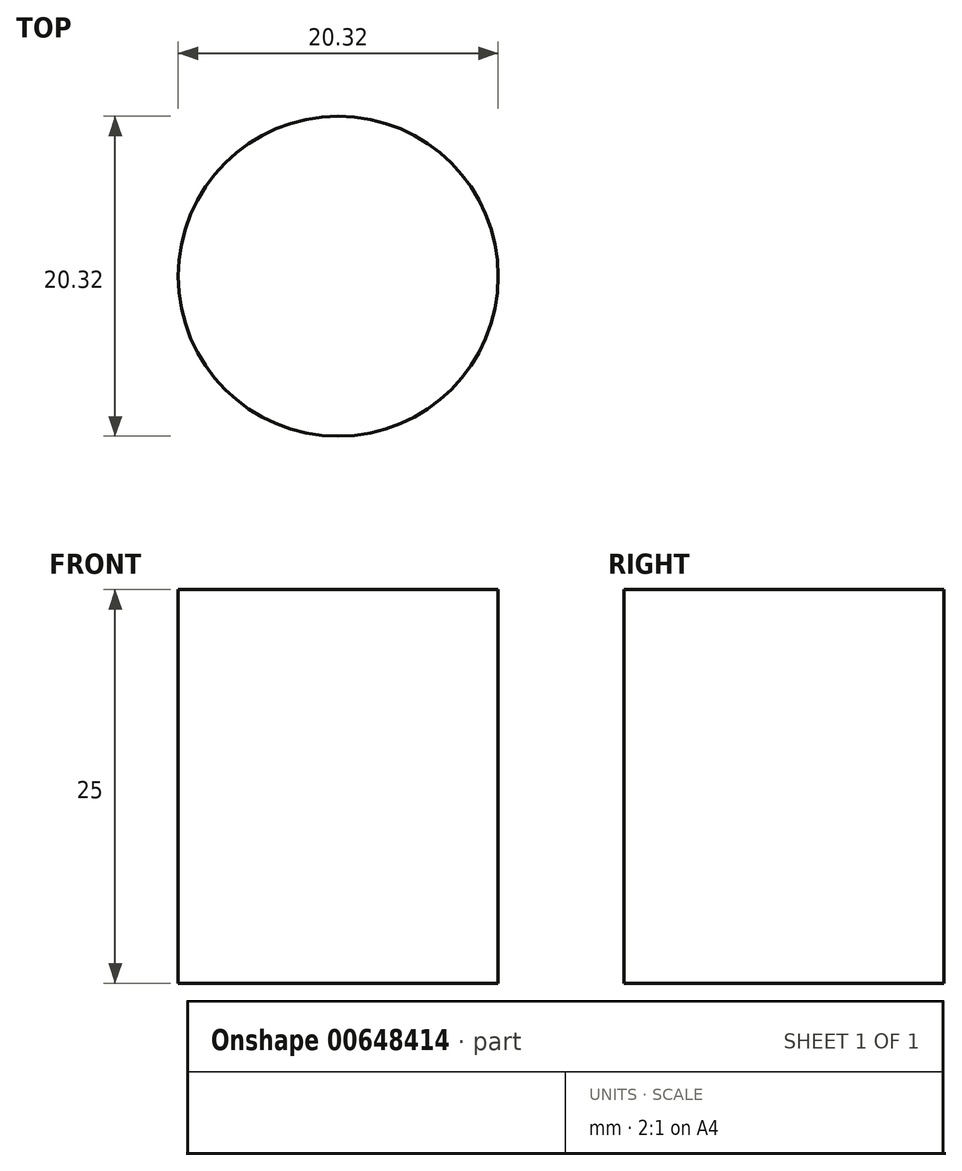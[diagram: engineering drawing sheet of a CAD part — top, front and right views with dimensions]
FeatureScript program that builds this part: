
annotation { "Feature Type Name" : "Feature", "Feature Type Description" : "" }
export const myFeature = defineFeature(function(context is Context, id is Id, definition is map)
    precondition{}
    {
        {
            var Q0;
            Q0=qCreatedBy(makeId("Top.planeOp"),FACE);
            var sketch = newSketch(context, id + "F0", { "sketchPlane" : qUnion([Q0])});
            skLineSegment(sketch, "E0.bottom", {"start": v(-40, -40) * mm, "end": v(40, -40) * mm, "construction": true});
            skLineSegment(sketch, "E0.top", {"start": v(-40, 40) * mm, "end": v(40, 40) * mm, "construction": true});
            skLineSegment(sketch, "E0.left", {"start": v(-40, -40) * mm, "end": v(-40, 40) * mm, "construction": true});
            skLineSegment(sketch, "E0.right", {"start": v(40, -40) * mm, "end": v(40, 40) * mm, "construction": true});
            skPoint(sketch, "E0.middle", {"position": v(0, 0) * mm});
            skCircle(sketch, "E1", {"center": v(40, 40) * mm, "radius": 7 * mm});
            skCircle(sketch, "E2", {"center": v(40, 40) * mm, "radius": 10.16 * mm});
            skLineSegment(sketch, "E3", {"start": v(23.61, 0) * mm, "end": v(23.61, 15.35) * mm});
            skLineSegment(sketch, "E4", {"start": v(22.84, 15.35) * mm, "end": v(14, 22.89) * mm});
            skLineSegment(sketch, "E5", {"start": v(14, 22.89) * mm, "end": v(12.44, 31.72) * mm});
            skLineSegment(sketch, "E6", {"start": v(12.44, 31.72) * mm, "end": v(34.1, 31.72) * mm});
            skLineSegment(sketch, "E7", {"start": v(34.1, 31.72) * mm, "end": v(128.15, 50) * mm});
            skSolve(sketch);
        }
        {
            var Q0;
            Q0=makeQuery(id+"F0.imprint","IMPRINT",FACE,{"disambiguationData":[TD([[makeQuery(id+"F0.imprint","IMPRINT",EDGE,{"derivedFrom":sQuery(id+"F0.wireOp",EDGE,"E1")}),1.0]])]});
            var Q1;
            {var subQ0=sQuery(id+"F0.wireOp",EDGE,"E1");Q1=makeQuery(id+"F0.imprint","IMPRINT",FACE,{"disambiguationData":[TD([[makeQuery(id+"F0.imprint","IMPRINT",EDGE,{"derivedFrom":subQ0}),-1.0]])]});}
            var Q2;
            {var subQ0=sQuery(id+"F0.wireOp",EDGE,"E7");var subQ1=sQuery(id+"F0.wireOp",EDGE,"E2");var subQ2=makeQuery(id+"F0.imprint","INTERSECT",VERTEX,{"disambiguationData":[OD(0.0)],"derivedFrom":[subQ1,subQ0]});Q2=makeQuery(id+"F0.imprint","IMPRINT",FACE,{"disambiguationData":[TD([[makeQuery(id+"F0.imprint","IMPRINT",EDGE,{"disambiguationData":[TD([[subQ2,-1.0]])],"derivedFrom":subQ1}),1.0]])]});}
            extrude(context, id + "F1", {"entities" : qUnion([Q0, Q1, Q2]), "depth" : 25 * mm, "offsetDistance" : 25 * mm});
        }
    });
